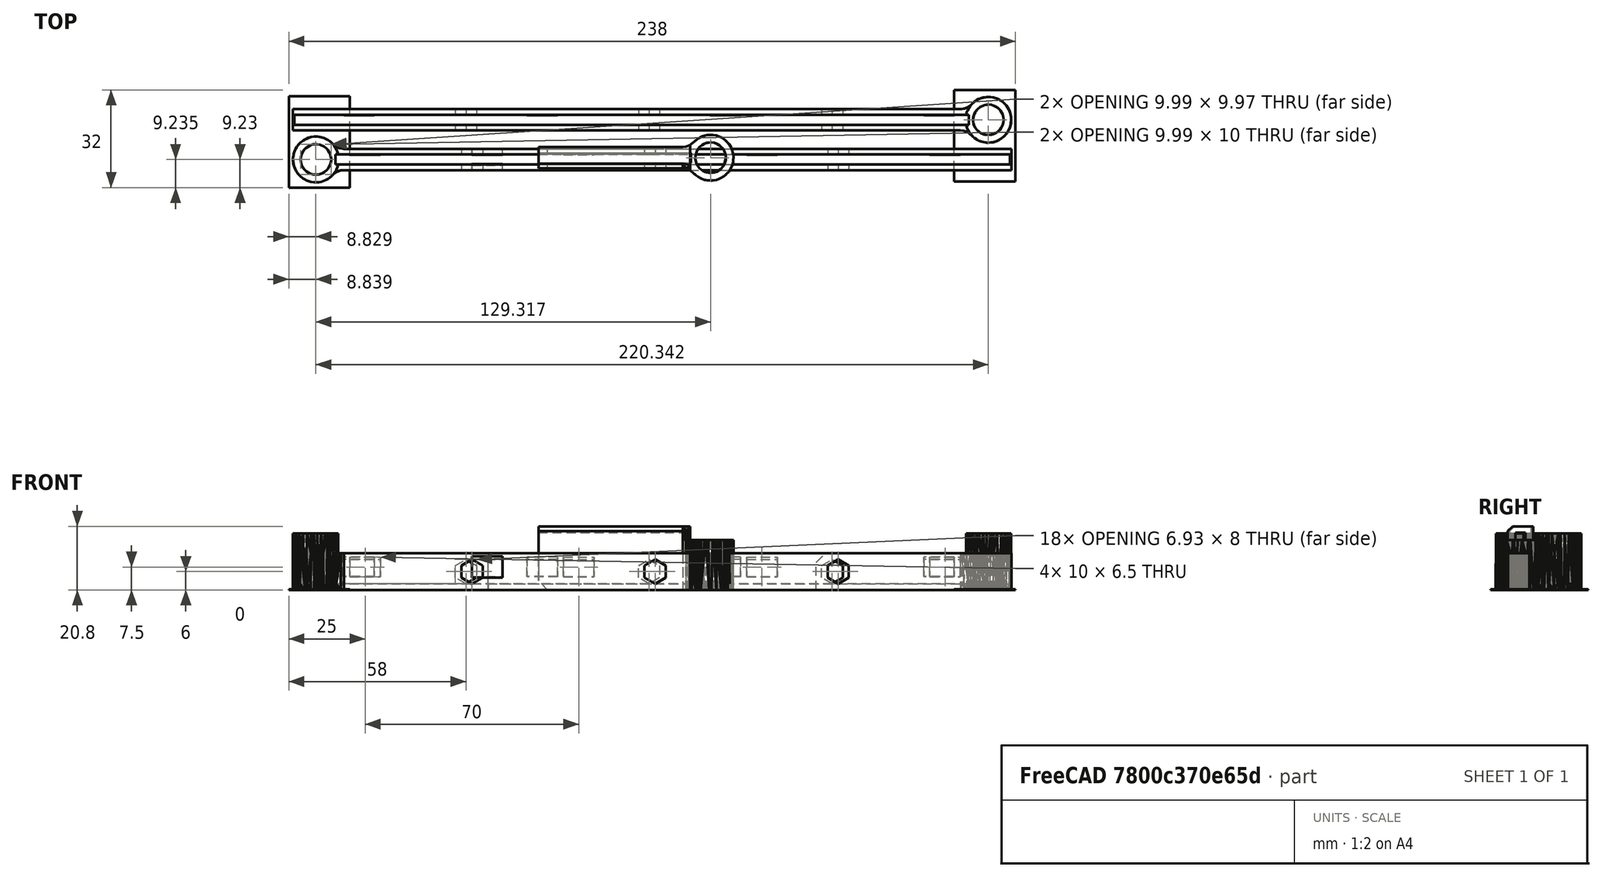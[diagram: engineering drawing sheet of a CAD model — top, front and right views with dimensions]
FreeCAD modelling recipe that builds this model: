
FCSTD DOCUMENT  (FreeCAD 0.18R14555 (Git shallow))
Label: hingle-extend
License: All rights reserved
LicenseURL: http://en.wikipedia.org/wiki/All_rights_reserved
objects: Part::Feature×12, Part::Box×10, Part::Chamfer×4, Part::MultiFuse×4, Part::Cut×3
note: 33 computed .brp shape members not serialized (recipe doc carries the construction recipe); baked Part::Feature solids carry a one-line shape summary decoded from their .brp

FEATURE [Part::Feature] top_handle001001_solid  label="top_handle002 (Solid)"
  Placement = pos=(0,-30.81,0) rot=(0,0,1;0rad)
  shape: bbox 63.91 x 14.98 x 18.5 mm, 326 faces (baked)
FEATURE [Part::Feature] bottom_handle001001_solid  label="bottom_handle002 (Solid)"
  Placement = pos=(0,-61.62,0) rot=(0,0,1;0rad)
  shape: bbox 63.91 x 14.99 x 20.8 mm, 256 faces (baked)
FEATURE [Part::Box] Box  label="Cube"
  AttacherType = Attacher::AttachEngine3D
  Height = 21
  Length = 51
  Placement = pos=(-44.76,1.58,2) rot=(0,0,1;0rad)
  Width = 3.3
FEATURE [Part::Box] Box001  label="Cube001"
  AttacherType = Attacher::AttachEngine3D
  Height = 18.8
  Length = 61
  Placement = pos=(10.75,2.16,0) rot=(0,0,1;0rad)
  Width = 3.3
FEATURE [Part::Cut] Cut001  label="bottom-33"
  Base = -> bottom_handle001001_solid
  Tool = -> Box001
FEATURE [Part::Cut] Cut
  Base = -> top_handle001001_solid
  Tool = -> Box
FEATURE [Part::Box] Box002  label="Cube002"
  AttacherType = Attacher::AttachEngine3D
  Height = 12
  Length = 221.5
  Placement = pos=(-44.76,-0.27,0) rot=(0,0,1;0rad)
  Width = 1.85
FEATURE [Part::Box] Box004  label="Cube004"
  AttacherType = Attacher::AttachEngine3D
  Height = 12
  Length = 221.5
  Placement = pos=(-44.76,4.88,0) rot=(0,0,1;0rad)
  Width = 1.85
FEATURE [Part::Box] Box005  label="Cube005"
  AttacherType = Attacher::AttachEngine3D
  Height = 2
  Length = 221
  Placement = pos=(-44.76,-0.27,0) rot=(0,0,1;0rad)
  Width = 7
FEATURE [Part::Box] Box006  label="Cube006"
  AttacherType = Attacher::AttachEngine3D
  Height = 12
  Length = 0.5
  Placement = pos=(176.24,-0.27,0) rot=(0,0,1;0rad)
  Width = 7
FEATURE [Part::Box] Box008  label="Cube008"
  AttacherType = Attacher::AttachEngine3D
  Height = 7
  Length = 10
  Placement = pos=(0,4.73,4) rot=(0,0,1;0rad)
  Width = 2
FEATURE [Part::Chamfer] Chamfer
  Base = -> Box008
  Edges = 1 edges: [Edge10 r1=1 r2=0.2]
FEATURE [Part::Box] Box007  label="Cube007"
  AttacherType = Attacher::AttachEngine3D
  Height = 7
  Length = 10
  Placement = pos=(0,-0.27,4) rot=(0,0,1;0rad)
  Width = 2
FEATURE [Part::Chamfer] Chamfer001
  Base = -> Box007
  Edges = 1 edges: [Edge12 r1=1 r2=0.2]
FEATURE [Part::Chamfer] Chamfer002
  Base = -> Chamfer
  Edges = 1 edges r=0.4: [Edge8]
FEATURE [Part::Chamfer] Chamfer003
  Base = -> Chamfer001
  Edges = 1 edges r=0.4: [Edge14]
FEATURE [Part::MultiFuse] Fusion001
  Shapes = -> [Box002,Box005,Cut,Box004,Box006]
FEATURE [Part::Feature] Chamfer002001  label="Chamfer005"
  Placement = pos=(-40,0,0) rot=(0,0,1;0rad)
  shape: bbox 10 x 2 x 7 mm, 8 faces (baked)
FEATURE [Part::Feature] Chamfer003014005  label="Chamfer006"
  Placement = pos=(30,0,0) rot=(0,0,1;0rad)
  shape: bbox 10 x 2 x 7 mm, 8 faces (baked)
FEATURE [Part::Feature] Chamfer003014006  label="Chamfer007"
  Placement = pos=(90,0,0) rot=(0,0,1;0rad)
  shape: bbox 10 x 2 x 7 mm, 8 faces (baked)
FEATURE [Part::Feature] Chamfer003014007  label="Chamfer008"
  Placement = pos=(150,0,0) rot=(0,0,1;0rad)
  shape: bbox 10 x 2 x 7 mm, 8 faces (baked)
FEATURE [Part::Feature] Body001
  Placement = pos=(0,9,6) rot=(0,0,1;0rad)
  shape: bbox 6.928 x 11 x 8 mm, 8 faces (baked)
FEATURE [Part::Feature] Body002
  Placement = pos=(60,9,6) rot=(0,0,1;0rad)
  shape: bbox 6.928 x 11 x 8 mm, 8 faces (baked)
FEATURE [Part::Feature] Body003
  Placement = pos=(120,9,6) rot=(0,0,1;0rad)
  shape: bbox 6.928 x 11 x 8 mm, 8 faces (baked)
FEATURE [Part::MultiFuse] Fusion002
  Shapes = -> [Body001,Body002,Body003]
FEATURE [Part::Cut] Cut002
  Base = -> Fusion001
  Tool = -> Fusion002
FEATURE [Part::MultiFuse] Fusion
  Shapes = -> [Chamfer003014006,Chamfer003014005,Chamfer002001,Chamfer003014007]
FEATURE [Part::MultiFuse] Fusion003
  Shapes = -> [Cut002,Fusion]
FEATURE [Part::Feature] Fusion003001  label="Fusion004"
  shape: bbox 235.4 x 14.98 x 18.5 mm, 383 faces (baked)
FEATURE [Part::Feature] Fusion003002  label="Fusion005"
  shape: bbox 235.4 x 14.98 x 18.5 mm, 383 faces (baked)
FEATURE [Part::Feature] Part__Mirroring001  label="Fusion005 (Mirror #1)001"
  Placement = pos=(118,13,0) rot=(0,0,1;0rad)
  shape: bbox 235.4 x 14.98 x 18.5 mm, 383 faces (baked)
FEATURE [Part::Box] Box009  label="Cube009"
  AttacherType = Attacher::AttachEngine3D
  Height = 0.2
  Length = 20
  Placement = pos=(-60,-6,0) rot=(0,0,1;0rad)
  Width = 30
FEATURE [Part::Box] Box010  label="Cube010"
  AttacherType = Attacher::AttachEngine3D
  Height = 0.2
  Length = 20
  Placement = pos=(158,-4,0) rot=(0,0,1;0rad)
  Width = 30
